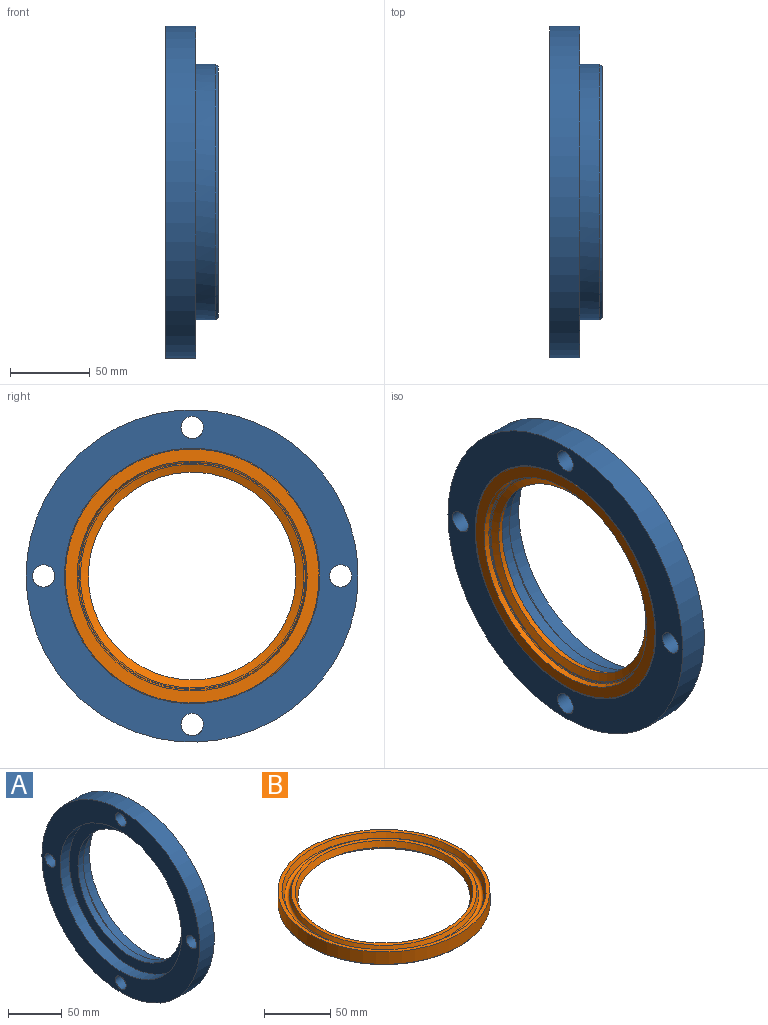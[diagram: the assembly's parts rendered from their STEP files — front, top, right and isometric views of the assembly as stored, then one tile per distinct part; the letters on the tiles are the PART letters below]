
ASSEMBLY  parts=2 mates=1
PART A: 16 faces, bbox 33.1x208x208 mm
  f0: cylinder r=68.5mm len=137mm, axis (1,0,0), area 3012.8mm2, adj f1,f8
  f1: plane 139x139mm, normal (1,0,0), area 433.5mm2, adj f0,f11
  f2: cylinder r=104mm len=208mm, axis (1,0,0), area 12415.6mm2, adj f3,f4
  f3: plane 208x208mm, normal (-1,0,0), area 13257.5mm2, adj f2,f9,f12,f13,f14,f15
  f4: plane 208x208mm, normal (1,0,0), area 13257.5mm2, adj f2,f6,f12,f13,f14,f15
  f5: cylinder r=74.5mm len=149mm, axis (-1,0,0), area 4259.7mm2, adj f7,f11
  f6: cylinder r=80mm len=160mm, axis (-1,0,0), area 6082.1mm2, adj f4,f10
  f7: plane 157.69x157.69mm, normal (1,0,0), area 2093.3mm2, adj f5,f10
  f8: plane 160x160mm, normal (-1,0,0), area 5365.1mm2, adj f0,f9
  f9: cylinder r=80mm len=160mm, axis (-1,0,0), area 6031.9mm2, adj f3,f8
  f10: cone r=78.85mm half-angle=30deg, axis (-1,0,0), area 1152.5mm2, adj f6,f7
  f11: torus R=69.5mm, axis (1,0,0), area 3586.8mm2, adj f1,f5
  f12: cylinder r=7mm len=19mm, axis (-1,0,0), area 835.7mm2, adj f3,f4
  f13: cylinder r=7mm len=19mm, axis (-1,0,0), area 835.7mm2, adj f3,f4
  f14: cylinder r=7mm len=19mm, axis (-1,0,0), area 835.7mm2, adj f3,f4
  f15: cylinder r=7mm len=19mm, axis (-1,0,0), area 835.7mm2, adj f3,f4
PART B: 13 faces, bbox 173.2x173.2x12 mm
  f0: cone r=77mm half-angle=22.5deg, axis (0,0,1), area 2322.3mm2, adj f1,f10
  f1: plane 160x160mm, normal (0,0,1), area 1479.7mm2, adj f0,f2
  f2: cylinder r=80mm len=160mm, axis (0,0,1), area 5780.5mm2, adj f1,f12
  f3: plane 159x159mm, normal (0,0,-1), area 3569.6mm2, adj f4,f12
  f4: cone r=71.29mm half-angle=10deg, axis (0,0,-1), area 1640.4mm2, adj f3,f11
  f5: plane 141.75x141.75mm, normal (0,0,-1), area 387.3mm2, adj f6,f11
  f6: cone r=65mm half-angle=68.2deg, axis (0,0,-1), area 2283.9mm2, adj f5,f7
  f7: cone r=67mm half-angle=21.8deg, axis (0,0,1), area 2233.2mm2, adj f6,f8
  f8: plane 140x140mm, normal (0,0,1), area 1291.2mm2, adj f7,f9
  f9: cone r=71.45mm half-angle=22.5deg, axis (0,0,-1), area 1678.1mm2, adj f8,f10
  f10: torus R=73.29mm, axis (0,0,1), area 2170.1mm2, adj f0,f9
  f11: torus R=70.88mm, axis (0,0,1), area 312.2mm2, adj f4,f5
  f12: torus R=79.5mm, axis (0,0,1), area 393.9mm2, adj f2,f3
PLACE A at identity fixed
PLACE B rot(axis=(0.58,0.58,0.58),120deg) t=(-19,0,0)mm
MATE fastened B.f0 <-> A.f0  axis (-1,0,0) through (-19,0,0)mm
